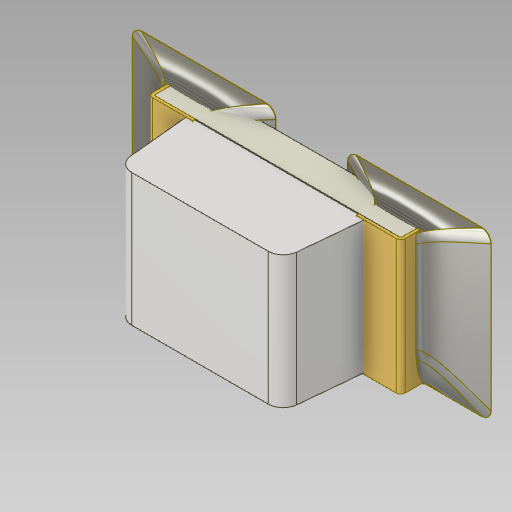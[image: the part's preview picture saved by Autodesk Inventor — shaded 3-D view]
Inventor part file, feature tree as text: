
AUTODESK INVENTOR PART (.ipt)
format: ipt  version: 2020 (Build 240168000, 168)  size: 448,512 bytes
history: native  units: in
note: dims shown in document units (in); Inventor stores cm internally (conversion verified against a paired STEP export)
features: sketch x3, imported_body x3, plane x2, extrude x1, fillet x1, loft x1, mirror x1, projected_geometry x1
ambient origin geometry x8: Origin, YZ Plane, XZ Plane, XY Plane, X Axis, Y Axis, Z Axis, Center Point
bodies: Solid1 (feature_tree), Solid2 (feature_tree), Solid3 (feature_tree)
feature tree (13):
  extrude  "Extrusion1"  Depth=0.0001in TaperAngle=0.0deg
  plane  "Work Plane1"
  fillet  "Fillet1"  [1 undecoded]
  loft  "Loft1"
  plane  "Work Plane2"
  mirror  "Mirror1"
  sketch  "Sketch1"  dims[d0=0.0433in d1=0.038in d2=0.0475in d3=0.0001in d4=0.0in d5=-0.002in]
  sketch  "Sketch2"  dims[d6=0.0005in d7=0.0025in]
  sketch  "Sketch3"  dims[d8=0.5906in d9=90.0deg d10=0.0in d11=90.0deg]
  projected_geometry  "Projected Loop1"
  imported_body  "Base1"
  imported_body  "Base2"
  imported_body  "Base3"
note: 1 required parameter value undecoded (feature->parameter linkage not recoverable at this tier; creation-order binding heuristic only, values carry confidence <= 0.55)
